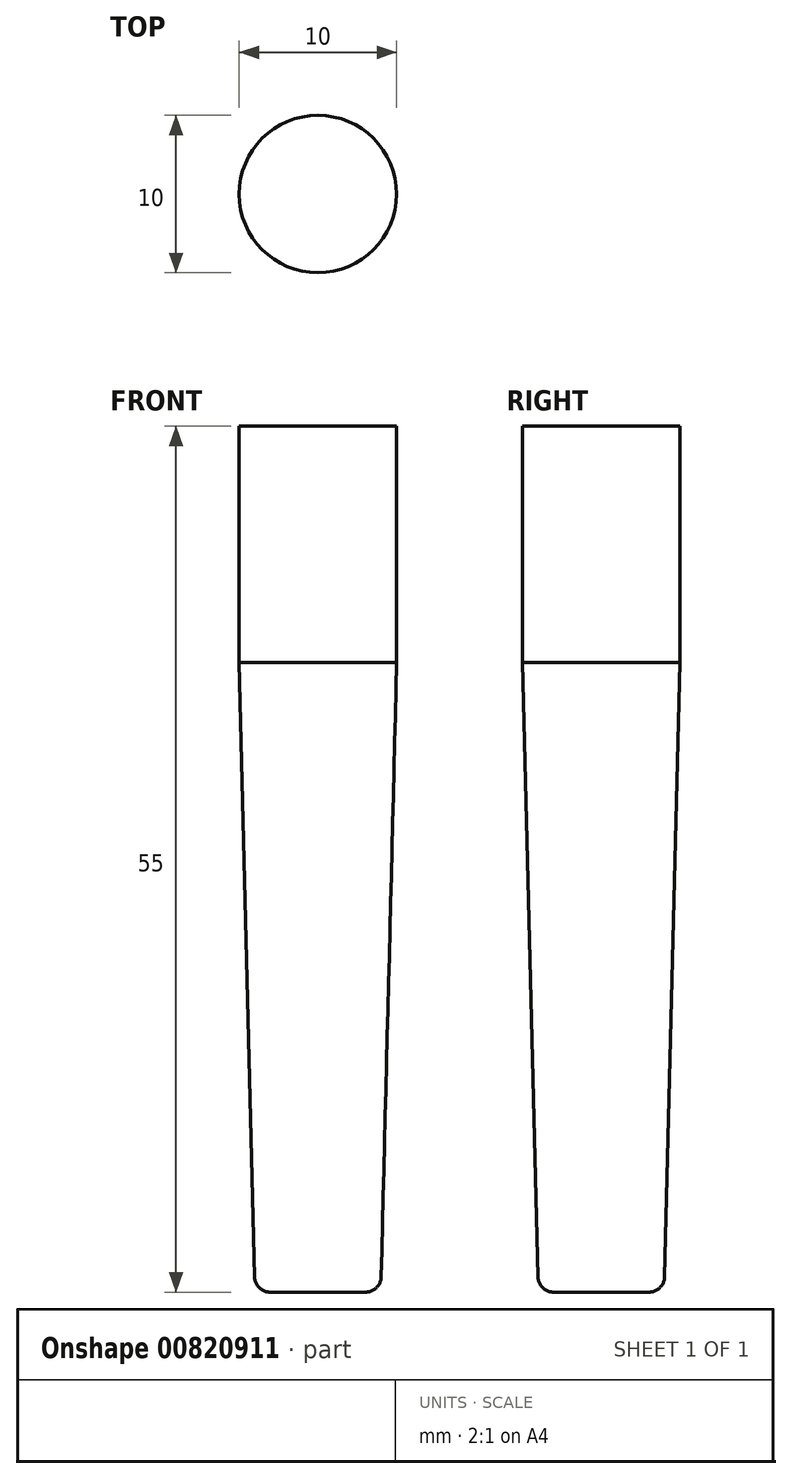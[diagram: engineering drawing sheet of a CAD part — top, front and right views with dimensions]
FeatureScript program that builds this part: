
annotation { "Feature Type Name" : "Feature", "Feature Type Description" : "" }
export const myFeature = defineFeature(function(context is Context, id is Id, definition is map)
    precondition{}
    {
        {
            var Q0;
            Q0=qCreatedBy(makeId("Top.planeOp"),FACE);
            var sketch = newSketch(context, id + "F0", { "sketchPlane" : qUnion([Q0])});
            skCircle(sketch, "E0", {"center": v(0, 0) * mm, "radius": 4 * mm});
            skSolve(sketch);
        }
        {
            var Q0;
            Q0=qCreatedBy(makeId("Top.planeOp"),FACE);
            cPlane(context, id + "F1", {"entities" : qUnion([Q0]), "cplaneType" : CPlaneType.OFFSET, "offset" : 40 * mm, "width" : 150 * mm, "height" : 150 * mm});
        }
        {
            var Q0;
            Q0=qCreatedBy(id+"F1.planeOp",FACE);
            var sketch = newSketch(context, id + "F2", { "sketchPlane" : qUnion([Q0])});
            skCircle(sketch, "E1", {"center": v(0, 0) * mm, "radius": 5 * mm});
            skSolve(sketch);
        }
        {
            var Q0;
            Q0=makeQuery(id+"F2.imprint","IMPRINT",FACE,{"disambiguationData":[TD([[makeQuery(id+"F2.imprint","IMPRINT",EDGE,{"derivedFrom":sQuery(id+"F2.wireOp",EDGE,"E1")}),1.0]])]});
            var Q1;
            Q1=makeQuery(id+"F0.imprint","IMPRINT",FACE,{"disambiguationData":[TD([[makeQuery(id+"F0.imprint","IMPRINT",EDGE,{"derivedFrom":sQuery(id+"F0.wireOp",EDGE,"E0")}),1.0]])]});
            loft(context, id + "F3", {"sheetProfilesArray" : [{ "sheetProfileEntities" : qUnion([Q0]) }, { "sheetProfileEntities" : qUnion([Q1]) }]});
        }
        {
            var Q0;
            Q0=makeQuery(id+"F3.opLoft","MID_CAP_EDGE",EDGE,{"disambiguationData":[OSD([sQuery(id+"F0.wireOp",EDGE,"E0")])],"capPos":1.0});
            fillet(context, id + "F4", {"entities" : qUnion([Q0]), "radius" : 1 * mm, "tangentPropagation" : true, "allowEdgeOverflow" : false});
        }
        {
            var Q0;
            Q0=makeQuery(id+"F3.opLoft","CAP_FACE",FACE,{"disambiguationData":[OSD([makeQuery(id+"F2.imprint","IMPRINT",FACE,{"disambiguationData":[TD([[makeQuery(id+"F2.imprint","IMPRINT",EDGE,{"derivedFrom":sQuery(id+"F2.wireOp",EDGE,"E1")}),1.0]])]})])],"isStart":true});
            var sketch = newSketch(context, id + "F5", { "sketchPlane" : qUnion([Q0])});
            skCircle(sketch, "E2", {"center": v(0, 0) * mm, "radius": 5 * mm});
            skSolve(sketch);
        }
        {
            var Q0;
            Q0 = qSketchRegion(id + "F5", true);
            extrude(context, id + "F6", {"entities" : qUnion([Q0]), "operationType" : NewBodyOperationType.ADD, "depth" : 15 * mm, "offsetDistance" : 25 * mm});
        }
    });
